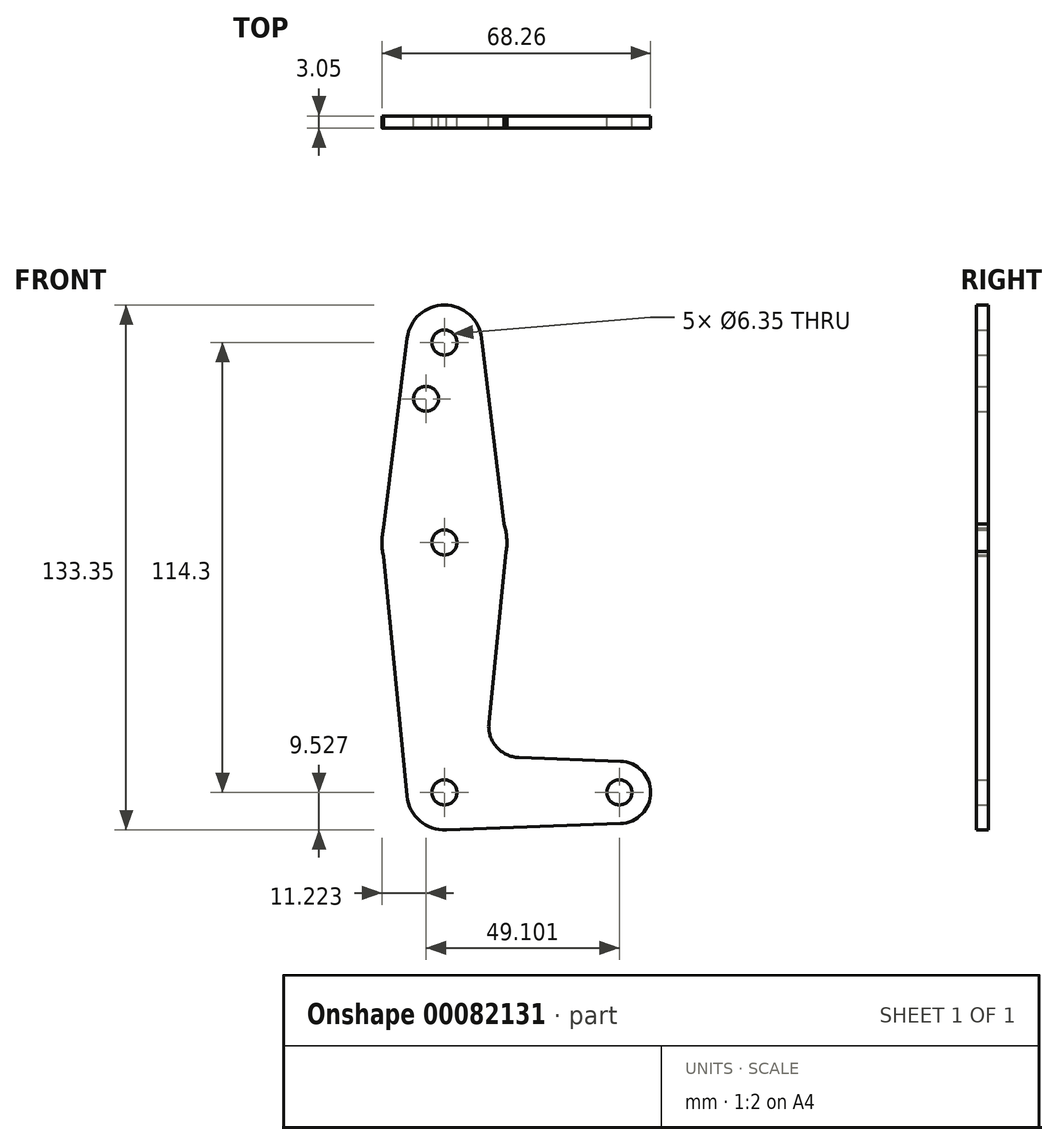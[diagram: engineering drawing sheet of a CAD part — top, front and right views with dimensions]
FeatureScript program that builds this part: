
annotation { "Feature Type Name" : "Feature", "Feature Type Description" : "" }
export const myFeature = defineFeature(function(context is Context, id is Id, definition is map)
    precondition{}
    {
        {
            var Q0;
            Q0=qCreatedBy(makeId("Front.planeOp"),FACE);
            var sketch = newSketch(context, id + "F0", { "sketchPlane" : qUnion([Q0])});
            skLineSegment(sketch, "E0", {"start": v(0, 114.28) * mm, "end": v(0, -0.02) * mm, "construction": true});
            skCircle(sketch, "E1", {"center": v(0, 114.28) * mm, "radius": 9.53 * mm});
            skCircle(sketch, "E2", {"center": v(0, 63.48) * mm, "radius": 15.88 * mm});
            skCircle(sketch, "E3", {"center": v(0, -0.02) * mm, "radius": 9.53 * mm});
            skLineSegment(sketch, "E4", {"start": v(0, -0.02) * mm, "end": v(44.44, -0.02) * mm, "construction": true});
            skCircle(sketch, "E5", {"center": v(44.44, -0.02) * mm, "radius": 7.94 * mm});
            skLineSegment(sketch, "E6", {"start": v(-9.46, 115.45) * mm, "end": v(-15.88, 63.75) * mm});
            skLineSegment(sketch, "E7", {"start": v(-15.88, 63.75) * mm, "end": v(-9.49, -0.96) * mm});
            skLineSegment(sketch, "E8", {"start": v(9.45, 115.42) * mm, "end": v(15.84, 62.6) * mm});
            skLineSegment(sketch, "E9", {"start": v(15.84, 62.6) * mm, "end": v(11.3, 17.57) * mm});
            skLineSegment(sketch, "E10", {"start": v(18.92, 8.83) * mm, "end": v(44.73, 7.9) * mm});
            skLineSegment(sketch, "E11", {"start": v(0.2, -9.55) * mm, "end": v(44.73, -7.96) * mm});
            skCircle(sketch, "E12", {"center": v(0, 114.28) * mm, "radius": 3.18 * mm});
            skCircle(sketch, "E13", {"center": v(0, 63.48) * mm, "radius": 3.17 * mm});
            skCircle(sketch, "E14", {"center": v(0, -0.02) * mm, "radius": 3.18 * mm});
            skCircle(sketch, "E15", {"center": v(44.44, -0.02) * mm, "radius": 3.18 * mm});
            skCircle(sketch, "E16", {"center": v(-4.66, 99.98) * mm, "radius": 3.18 * mm});
            skArc(sketch, "E17.filletArc", {"start": v(11.3, 17.57) * mm, "mid": v(13.21, 11.55) * mm, "end": v(18.92, 8.83) * mm});
            skSolve(sketch);
        }
        {
            var Q0;
            Q0 = qSketchRegion(id + "F0", true);
            extrude(context, id + "F1", {"entities" : qUnion([Q0]), "depth" : 3.05 * mm});
        }
    });
